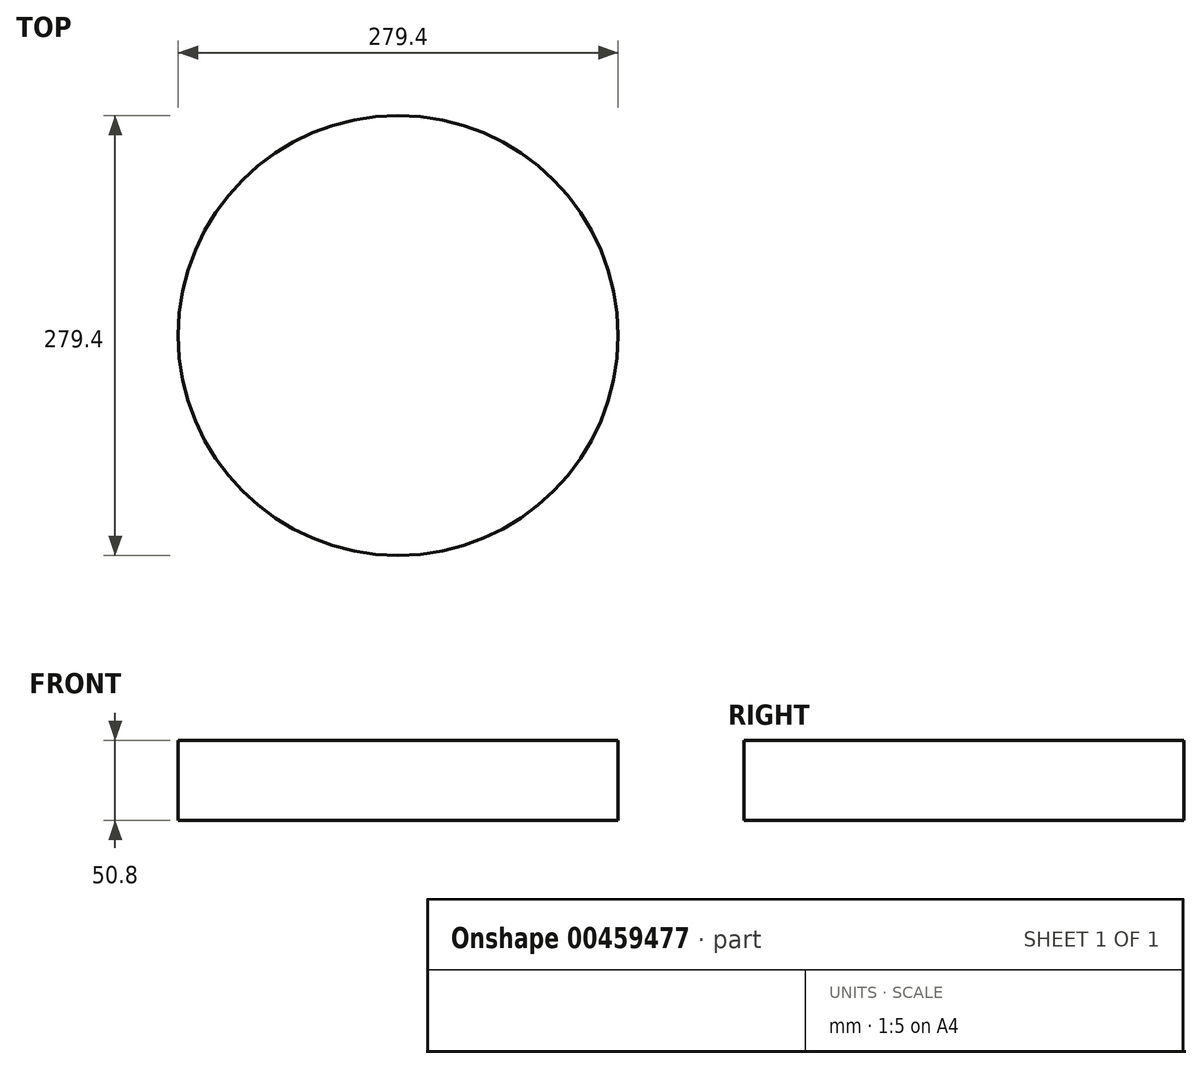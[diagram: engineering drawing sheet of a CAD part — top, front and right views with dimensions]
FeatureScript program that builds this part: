
annotation { "Feature Type Name" : "Feature", "Feature Type Description" : "" }
export const myFeature = defineFeature(function(context is Context, id is Id, definition is map)
    precondition{}
    {
        {
            var Q0;
            Q0=qCreatedBy(makeId("Top.planeOp"),FACE);
            var sketch = newSketch(context, id + "F0", { "sketchPlane" : qUnion([Q0])});
            skCircle(sketch, "E0", {"center": v(0, 0) * mm, "radius": 139.7 * mm});
            skSolve(sketch);
        }
        {
            var Q0;
            Q0=makeQuery(id+"F0.imprint","IMPRINT",FACE,{"disambiguationData":[TD([[makeQuery(id+"F0.imprint","IMPRINT",EDGE,{"derivedFrom":sQuery(id+"F0.wireOp",EDGE,"E0")}),1.0]])]});
            extrude(context, id + "F1", {"entities" : qUnion([Q0]), "depth" : 50.8 * mm});
        }
    });
